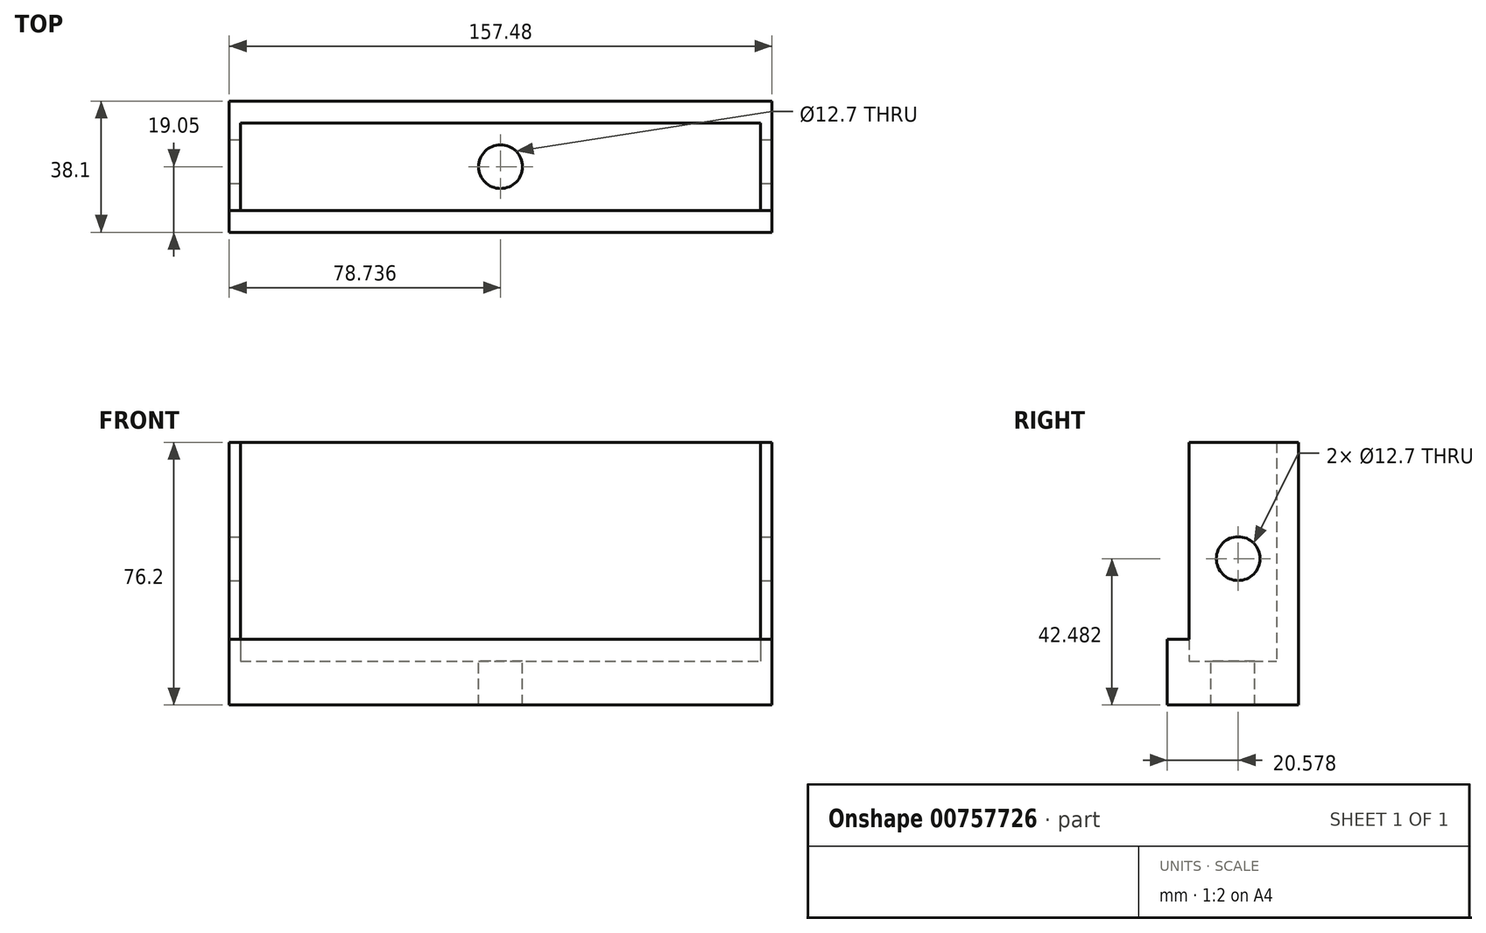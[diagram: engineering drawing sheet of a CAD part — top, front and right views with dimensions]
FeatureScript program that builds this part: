
annotation { "Feature Type Name" : "Feature", "Feature Type Description" : "" }
export const myFeature = defineFeature(function(context is Context, id is Id, definition is map)
    precondition{}
    {
        {
            var Q0;
            Q0=qCreatedBy(makeId("Front.planeOp"),FACE);
            var sketch = newSketch(context, id + "F0", { "sketchPlane" : qUnion([Q0])});
            skLineSegment(sketch, "E0.bottom", {"start": v(-95.5, 25.19) * mm, "end": v(61.99, 25.19) * mm});
            skLineSegment(sketch, "E0.top", {"start": v(-95.5, -51.01) * mm, "end": v(61.99, -51.01) * mm});
            skLineSegment(sketch, "E0.left", {"start": v(-95.5, 25.19) * mm, "end": v(-95.5, -51.01) * mm});
            skLineSegment(sketch, "E0.right", {"start": v(61.99, 25.19) * mm, "end": v(61.99, -51.01) * mm});
            skSolve(sketch);
        }
        {
            var Q0;
            Q0=makeQuery(id+"F0.imprint","IMPRINT",FACE,{"disambiguationData":[TD([[makeQuery(id+"F0.imprint","IMPRINT",EDGE,{"derivedFrom":sQuery(id+"F0.wireOp",EDGE,"E0.bottom")}),-1.0]])]});
            extrude(context, id + "F1", {"entities" : qUnion([Q0]), "depth" : 6.35 * mm, "offsetDistance" : 25.4 * mm});
        }
        {
            var Q0;
            Q0=makeQuery(id+"F1.opExtrude","CAP_FACE",FACE,{"disambiguationData":[OSD([sQuery(id+"F0.wireOp",EDGE,"E0.bottom"),sQuery(id+"F0.wireOp",EDGE,"E0.top"),sQuery(id+"F0.wireOp",EDGE,"E0.left"),sQuery(id+"F0.wireOp",EDGE,"E0.right")])],"isStart":false});
            var sketch = newSketch(context, id + "F2", { "sketchPlane" : qUnion([Q0])});
            skLineSegment(sketch, "E1.bottom", {"start": v(-95.5, -51.01) * mm, "end": v(61.99, -51.01) * mm});
            skLineSegment(sketch, "E1.top", {"start": v(-95.5, -38.31) * mm, "end": v(61.99, -38.31) * mm});
            skLineSegment(sketch, "E1.left", {"start": v(-95.5, -51.01) * mm, "end": v(-95.5, -38.31) * mm});
            skLineSegment(sketch, "E1.right", {"start": v(61.99, -51.01) * mm, "end": v(61.99, -38.31) * mm});
            skSolve(sketch);
        }
        {
            var Q0;
            Q0=makeQuery(id+"F2.imprint","IMPRINT",FACE,{"disambiguationData":[TD([[makeQuery(id+"F2.imprint","IMPRINT",EDGE,{"derivedFrom":sQuery(id+"F2.wireOp",EDGE,"E1.bottom")}),1.0]])]});
            extrude(context, id + "F3", {"entities" : qUnion([Q0]), "operationType" : NewBodyOperationType.ADD, "depth" : 31.75 * mm, "offsetDistance" : 25.4 * mm});
        }
        {
            var Q0;
            Q0=makeQuery(id+"F3.opExtrude","SWEPT_FACE",FACE,{"disambiguationData":[OSD([sQuery(id+"F2.wireOp",EDGE,"E1.top")])]});
            var sketch = newSketch(context, id + "F4", { "sketchPlane" : qUnion([Q0])});
            skLineSegment(sketch, "E2.bottom", {"start": v(-95.5, -38.1) * mm, "end": v(61.99, -38.1) * mm});
            skLineSegment(sketch, "E2.top", {"start": v(-95.5, -31.75) * mm, "end": v(61.99, -31.75) * mm});
            skLineSegment(sketch, "E2.left", {"start": v(-95.5, -38.1) * mm, "end": v(-95.5, -31.75) * mm});
            skLineSegment(sketch, "E2.right", {"start": v(61.99, -38.1) * mm, "end": v(61.99, -31.75) * mm});
            skSolve(sketch);
        }
        {
            var Q0;
            Q0=makeQuery(id+"F4.imprint","IMPRINT",FACE,{"disambiguationData":[TD([[makeQuery(id+"F4.imprint","IMPRINT",EDGE,{"derivedFrom":sQuery(id+"F4.wireOp",EDGE,"E2.bottom")}),1.0]])]});
            extrude(context, id + "F5", {"entities" : qUnion([Q0]), "operationType" : NewBodyOperationType.ADD, "depth" : 6.35 * mm, "offsetDistance" : 25.4 * mm});
        }
        {
            var Q0;
            Q0=makeQuery(id+"F3.opExtrude","SWEPT_FACE",FACE,{"disambiguationData":[OSD([sQuery(id+"F2.wireOp",EDGE,"E1.top")])]});
            var sketch = newSketch(context, id + "F6", { "sketchPlane" : qUnion([Q0])});
            skLineSegment(sketch, "E3", {"start": v(-95.5, -19.05) * mm, "end": v(61.99, -19.05) * mm});
            skPoint(sketch, "E4", {"position": v(-16.75, -19.05) * mm});
            skSolve(sketch);
        }
        {
            var Q0;
            Q0=sQuery(id+"F6.wireOp",VERTEX,"E4");
            var Q1;
            Q1=makeQuery(id+"F1.opExtrude","SWEPT_BODY",BODY,{"disambiguationData":[OSD([sQuery(id+"F0.wireOp",EDGE,"E0.bottom"),sQuery(id+"F0.wireOp",EDGE,"E0.top"),sQuery(id+"F0.wireOp",EDGE,"E0.left"),sQuery(id+"F0.wireOp",EDGE,"E0.right")])]});
            hole(context, id + "F7", {"style" : HoleStyle.SIMPLE, "endStyle" : HoleEndStyle.THROUGH, "holeDiameter" : 12.7 * mm, "majorDiameter" : 6.35 * mm, "isTappedThrough" : true, "tappedDepth" : 12.7 * mm, "tapClearance" : 3, "locations" : qUnion([Q0]), "scope" : qUnion([Q1])});
        }
        {
            var Q0;
            Q0=makeQuery(id+"F1.opExtrude","CAP_FACE",FACE,{"disambiguationData":[OSD([sQuery(id+"F0.wireOp",EDGE,"E0.bottom"),sQuery(id+"F0.wireOp",EDGE,"E0.top"),sQuery(id+"F0.wireOp",EDGE,"E0.left"),sQuery(id+"F0.wireOp",EDGE,"E0.right")])],"isStart":false});
            var sketch = newSketch(context, id + "F8", { "sketchPlane" : qUnion([Q0])});
            skLineSegment(sketch, "E5.bottom", {"start": v(-95.5, 25.19) * mm, "end": v(-92.2, 25.19) * mm});
            skLineSegment(sketch, "E5.top", {"start": v(-95.5, -38.31) * mm, "end": v(-92.2, -38.31) * mm});
            skLineSegment(sketch, "E5.left", {"start": v(-95.5, 25.19) * mm, "end": v(-95.5, -38.31) * mm});
            skLineSegment(sketch, "E5.right", {"start": v(-92.2, 25.19) * mm, "end": v(-92.2, -38.31) * mm});
            skLineSegment(sketch, "E6.bottom", {"start": v(61.99, 25.19) * mm, "end": v(58.68, 25.19) * mm});
            skLineSegment(sketch, "E6.top", {"start": v(61.99, -38.31) * mm, "end": v(58.68, -38.31) * mm});
            skLineSegment(sketch, "E6.left", {"start": v(61.99, 25.19) * mm, "end": v(61.99, -38.31) * mm});
            skLineSegment(sketch, "E6.right", {"start": v(58.68, 25.19) * mm, "end": v(58.68, -38.31) * mm});
            skSolve(sketch);
        }
        {
            var Q0;
            Q0=makeQuery(id+"F8.imprint","IMPRINT",FACE,{"disambiguationData":[TD([[makeQuery(id+"F8.imprint","IMPRINT",EDGE,{"derivedFrom":sQuery(id+"F8.wireOp",EDGE,"E5.bottom")}),-1.0]])]});
            var Q1;
            Q1=makeQuery(id+"F8.imprint","IMPRINT",FACE,{"disambiguationData":[TD([[makeQuery(id+"F8.imprint","IMPRINT",EDGE,{"derivedFrom":sQuery(id+"F8.wireOp",EDGE,"E6.bottom")}),-1.0]])]});
            extrude(context, id + "F9", {"entities" : qUnion([Q0, Q1]), "operationType" : NewBodyOperationType.ADD, "depth" : 25.4 * mm, "offsetDistance" : 25.4 * mm});
        }
        {
            var Q0;
            Q0=makeQuery(id+"F9.boolean.opBoolean","MERGE",FACE,{"derivedFrom":[makeQuery(id+"F5.boolean.opBoolean","MERGE",FACE,{"derivedFrom":[makeQuery(id+"F3.boolean.opBoolean","MERGE",FACE,{"derivedFrom":[makeQuery(id+"F1.opExtrude","SWEPT_FACE",FACE,{"disambiguationData":[OSD([sQuery(id+"F0.wireOp",EDGE,"E0.right")])]}),makeQuery(id+"F3.opExtrude","SWEPT_FACE",FACE,{"disambiguationData":[OSD([sQuery(id+"F2.wireOp",EDGE,"E1.right")])]})]}),makeQuery(id+"F5.opExtrude","SWEPT_FACE",FACE,{"disambiguationData":[OSD([sQuery(id+"F4.wireOp",EDGE,"E2.right")])]})]}),makeQuery(id+"F9.opExtrude","SWEPT_FACE",FACE,{"disambiguationData":[OSD([sQuery(id+"F8.wireOp",EDGE,"E6.left")])]})]});
            var sketch = newSketch(context, id + "F10", { "sketchPlane" : qUnion([Q0])});
            skPoint(sketch, "E7", {"position": v(-17.52, -8.53) * mm});
            skSolve(sketch);
        }
        {
            var Q0;
            Q0=sQuery(id+"F10.wireOp",VERTEX,"E7");
            var Q1;
            Q1=makeQuery(id+"F1.opExtrude","SWEPT_BODY",BODY,{"disambiguationData":[OSD([sQuery(id+"F0.wireOp",EDGE,"E0.bottom"),sQuery(id+"F0.wireOp",EDGE,"E0.top"),sQuery(id+"F0.wireOp",EDGE,"E0.left"),sQuery(id+"F0.wireOp",EDGE,"E0.right")])]});
            hole(context, id + "F11", {"style" : HoleStyle.SIMPLE, "endStyle" : HoleEndStyle.THROUGH, "holeDiameter" : 12.7 * mm, "majorDiameter" : 6.35 * mm, "isTappedThrough" : true, "tappedDepth" : 12.7 * mm, "tapClearance" : 3, "locations" : qUnion([Q0]), "scope" : qUnion([Q1])});
        }
    });
